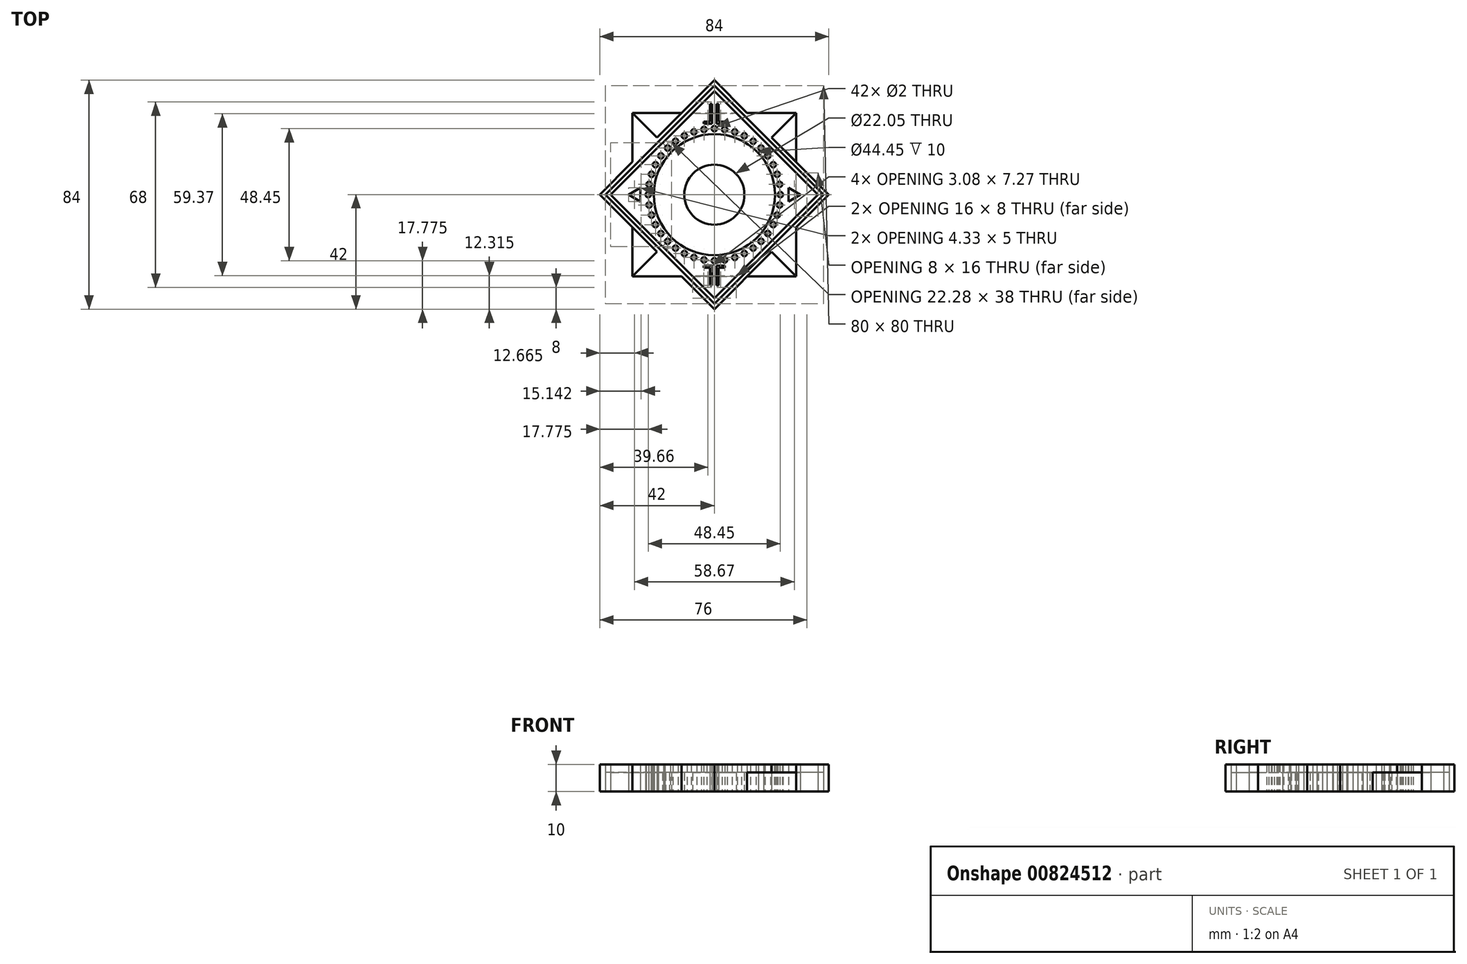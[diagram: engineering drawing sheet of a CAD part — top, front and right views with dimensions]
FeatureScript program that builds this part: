
annotation { "Feature Type Name" : "Feature", "Feature Type Description" : "" }
export const myFeature = defineFeature(function(context is Context, id is Id, definition is map)
    precondition{}
    {
        {
            var Q0;
            Q0=qCreatedBy(makeId("Top.planeOp"),FACE);
            var sketch = newSketch(context, id + "F0", { "sketchPlane" : qUnion([Q0])});
            skCircle(sketch, "E0", {"center": v(0, 0) * mm, "radius": 11.03 * mm});
            skCircle(sketch, "E1", {"center": v(0, 0) * mm, "radius": 22.23 * mm});
            skLineSegment(sketch, "E2.bottom", {"start": v(-30, -30) * mm, "end": v(30, -30) * mm});
            skLineSegment(sketch, "E2.top", {"start": v(-30, 30) * mm, "end": v(30, 30) * mm});
            skLineSegment(sketch, "E2.left", {"start": v(-30, -30) * mm, "end": v(-30, 30) * mm});
            skLineSegment(sketch, "E2.right", {"start": v(30, -30) * mm, "end": v(30, 30) * mm});
            skLineSegment(sketch, "E3", {"start": v(0, 42) * mm, "end": v(-42, 0) * mm});
            skLineSegment(sketch, "E4", {"start": v(-42, 0) * mm, "end": v(0, -42) * mm});
            skLineSegment(sketch, "E5", {"start": v(0, -42) * mm, "end": v(42, 0) * mm});
            skLineSegment(sketch, "E6", {"start": v(42, 0) * mm, "end": v(0, 42) * mm});
            skLineSegment(sketch, "E7", {"start": v(-30, 30) * mm, "end": v(30, -30) * mm});
            skLineSegment(sketch, "E8", {"start": v(-30, -30) * mm, "end": v(30, 30) * mm});
            skLineSegment(sketch, "E9", {"start": v(-40, 0) * mm, "end": v(0, 40) * mm});
            skLineSegment(sketch, "E10", {"start": v(0, 40) * mm, "end": v(40, 0) * mm});
            skLineSegment(sketch, "E11", {"start": v(40, 0) * mm, "end": v(0, -40) * mm});
            skLineSegment(sketch, "E12", {"start": v(0, -40) * mm, "end": v(-40, 0) * mm});
            skLineSegment(sketch, "E13", {"start": v(0, 38) * mm, "end": v(-38, 0) * mm});
            skPoint(sketch, "E13.startSnap0", {"position": v(0, 30) * mm});
            skPoint(sketch, "E13.endSnap0", {"position": v(-30, 0) * mm});
            skLineSegment(sketch, "E14", {"start": v(-38, 0) * mm, "end": v(0, -38) * mm});
            skLineSegment(sketch, "E15", {"start": v(0, -38) * mm, "end": v(38, 0) * mm});
            skLineSegment(sketch, "E16", {"start": v(38, 0) * mm, "end": v(0, 38) * mm});
            skCircle(sketch, "E17", {"center": v(0, 24.23) * mm, "radius": 1 * mm});
            skCircle(sketch, "E18.1.0", {"center": v(-3.79, 23.93) * mm, "radius": 1 * mm});
            skCircle(sketch, "E18.2.0", {"center": v(-7.49, 23.04) * mm, "radius": 1 * mm});
            skCircle(sketch, "E18.3.0", {"center": v(-11, 21.58) * mm, "radius": 1 * mm});
            skCircle(sketch, "E18.4.0", {"center": v(-14.24, 19.6) * mm, "radius": 1 * mm});
            skCircle(sketch, "E18.5.0", {"center": v(-17.13, 17.13) * mm, "radius": 1 * mm});
            skCircle(sketch, "E18.6.0", {"center": v(-19.6, 14.24) * mm, "radius": 1 * mm});
            skCircle(sketch, "E18.7.0", {"center": v(-21.58, 11) * mm, "radius": 1 * mm});
            skCircle(sketch, "E18.8.0", {"center": v(-23.04, 7.49) * mm, "radius": 1 * mm});
            skCircle(sketch, "E18.9.0", {"center": v(-23.93, 3.79) * mm, "radius": 1 * mm});
            skCircle(sketch, "E18.10.0", {"center": v(-24.23, 0) * mm, "radius": 1 * mm});
            skCircle(sketch, "E18.11.0", {"center": v(-23.93, -3.79) * mm, "radius": 1 * mm});
            skCircle(sketch, "E18.12.0", {"center": v(-23.04, -7.49) * mm, "radius": 1 * mm});
            skCircle(sketch, "E18.13.0", {"center": v(-21.58, -11) * mm, "radius": 1 * mm});
            skCircle(sketch, "E18.14.0", {"center": v(-19.6, -14.24) * mm, "radius": 1 * mm});
            skCircle(sketch, "E18.15.0", {"center": v(-17.13, -17.13) * mm, "radius": 1 * mm});
            skCircle(sketch, "E18.16.0", {"center": v(-14.24, -19.6) * mm, "radius": 1 * mm});
            skCircle(sketch, "E18.17.0", {"center": v(-11, -21.58) * mm, "radius": 1 * mm});
            skCircle(sketch, "E18.18.0", {"center": v(-7.49, -23.04) * mm, "radius": 1 * mm});
            skCircle(sketch, "E18.19.0", {"center": v(-3.79, -23.93) * mm, "radius": 1 * mm});
            skCircle(sketch, "E18.20.0", {"center": v(0, -24.23) * mm, "radius": 1 * mm});
            skCircle(sketch, "E18.21.0", {"center": v(3.79, -23.93) * mm, "radius": 1 * mm});
            skCircle(sketch, "E18.22.0", {"center": v(7.49, -23.04) * mm, "radius": 1 * mm});
            skCircle(sketch, "E18.23.0", {"center": v(11, -21.58) * mm, "radius": 1 * mm});
            skCircle(sketch, "E18.24.0", {"center": v(14.24, -19.6) * mm, "radius": 1 * mm});
            skCircle(sketch, "E18.25.0", {"center": v(17.13, -17.13) * mm, "radius": 1 * mm});
            skCircle(sketch, "E18.26.0", {"center": v(19.6, -14.24) * mm, "radius": 1 * mm});
            skCircle(sketch, "E18.27.0", {"center": v(21.58, -11) * mm, "radius": 1 * mm});
            skCircle(sketch, "E18.28.0", {"center": v(23.04, -7.49) * mm, "radius": 1 * mm});
            skCircle(sketch, "E18.29.0", {"center": v(23.93, -3.79) * mm, "radius": 1 * mm});
            skCircle(sketch, "E18.30.0", {"center": v(24.23, 0) * mm, "radius": 1 * mm});
            skCircle(sketch, "E18.31.0", {"center": v(23.93, 3.79) * mm, "radius": 1 * mm});
            skCircle(sketch, "E18.32.0", {"center": v(23.04, 7.49) * mm, "radius": 1 * mm});
            skCircle(sketch, "E18.33.0", {"center": v(21.58, 11) * mm, "radius": 1 * mm});
            skCircle(sketch, "E18.34.0", {"center": v(19.6, 14.24) * mm, "radius": 1 * mm});
            skCircle(sketch, "E18.35.0", {"center": v(17.13, 17.13) * mm, "radius": 1 * mm});
            skCircle(sketch, "E18.36.0", {"center": v(14.24, 19.6) * mm, "radius": 1 * mm});
            skCircle(sketch, "E18.37.0", {"center": v(11, 21.58) * mm, "radius": 1 * mm});
            skCircle(sketch, "E18.38.0", {"center": v(7.49, 23.04) * mm, "radius": 1 * mm});
            skCircle(sketch, "E18.39.0", {"center": v(3.79, 23.93) * mm, "radius": 1 * mm});
            skLineSegment(sketch, "E19", {"start": v(-31.5, 0) * mm, "end": v(-27.17, 2.5) * mm});
            skLineSegment(sketch, "E20", {"start": v(-27.17, 2.5) * mm, "end": v(-27.17, -2.5) * mm});
            skLineSegment(sketch, "E21", {"start": v(-27.17, -2.5) * mm, "end": v(-31.5, 0) * mm});
            skLineSegment(sketch, "E22.1.0", {"start": v(27.17, -2.5) * mm, "end": v(27.17, 2.5) * mm});
            skLineSegment(sketch, "E22.1.1", {"start": v(31.5, 0) * mm, "end": v(27.17, -2.5) * mm});
            skLineSegment(sketch, "E22.1.2", {"start": v(27.17, 2.5) * mm, "end": v(31.5, 0) * mm});
            skLineSegment(sketch, "E23", {"start": v(-3.88, -26.05) * mm, "end": v(-0.8, -26.05) * mm});
            skLineSegment(sketch, "E24", {"start": v(-0.8, -26.05) * mm, "end": v(-0.8, -33.32) * mm});
            skLineSegment(sketch, "E25", {"start": v(-0.8, -33.32) * mm, "end": v(-1.6, -33.32) * mm});
            skLineSegment(sketch, "E26", {"start": v(-3.88, -26.05) * mm, "end": v(-3.88, -26.85) * mm});
            skLineSegment(sketch, "E27", {"start": v(-3.88, -26.85) * mm, "end": v(-1.6, -26.85) * mm});
            skLineSegment(sketch, "E28", {"start": v(-1.6, -26.85) * mm, "end": v(-1.6, -33.32) * mm});
            skLineSegment(sketch, "E29.MirrorCS", {"start": v(0.8, -33.32) * mm, "end": v(1.6, -33.32) * mm});
            skLineSegment(sketch, "E30.MirrorCS", {"start": v(0.8, -26.05) * mm, "end": v(0.8, -33.32) * mm});
            skLineSegment(sketch, "E31.MirrorCS", {"start": v(3.88, -26.05) * mm, "end": v(0.8, -26.05) * mm});
            skLineSegment(sketch, "E32.MirrorCS", {"start": v(3.88, -26.05) * mm, "end": v(3.88, -26.85) * mm});
            skLineSegment(sketch, "E33.MirrorCS", {"start": v(1.6, -26.85) * mm, "end": v(1.6, -33.32) * mm});
            skLineSegment(sketch, "E34.MirrorCS", {"start": v(3.88, -26.85) * mm, "end": v(1.6, -26.85) * mm});
            skLineSegment(sketch, "E35.MirrorCS", {"start": v(3.88, 26.05) * mm, "end": v(0.8, 26.05) * mm});
            skLineSegment(sketch, "E36.MirrorCS", {"start": v(3.88, 26.05) * mm, "end": v(3.88, 26.85) * mm});
            skLineSegment(sketch, "E37.MirrorCS", {"start": v(3.88, 26.85) * mm, "end": v(1.6, 26.85) * mm});
            skLineSegment(sketch, "E38.MirrorCS", {"start": v(1.6, 26.85) * mm, "end": v(1.6, 33.32) * mm});
            skLineSegment(sketch, "E39.MirrorCS", {"start": v(0.8, 26.05) * mm, "end": v(0.8, 33.32) * mm});
            skLineSegment(sketch, "E40.MirrorCS", {"start": v(0.8, 33.32) * mm, "end": v(1.6, 33.32) * mm});
            skLineSegment(sketch, "E41.MirrorCS", {"start": v(-0.8, 33.32) * mm, "end": v(-1.6, 33.32) * mm});
            skLineSegment(sketch, "E42.MirrorCS", {"start": v(-1.6, 26.85) * mm, "end": v(-1.6, 33.32) * mm});
            skLineSegment(sketch, "E43.MirrorCS", {"start": v(-0.8, 26.05) * mm, "end": v(-0.8, 33.32) * mm});
            skLineSegment(sketch, "E44.MirrorCS", {"start": v(-3.88, 26.05) * mm, "end": v(-0.8, 26.05) * mm});
            skLineSegment(sketch, "E45.MirrorCS", {"start": v(-3.88, 26.85) * mm, "end": v(-1.6, 26.85) * mm});
            skLineSegment(sketch, "E46.MirrorCS", {"start": v(-3.88, 26.05) * mm, "end": v(-3.88, 26.85) * mm});
            skSolve(sketch);
        }
        {
            var Q0;
            Q0=makeQuery(id+"F0.imprint","IMPRINT",FACE,{"disambiguationData":[TD([[makeQuery(id+"F0.imprint","IMPRINT",EDGE,{"derivedFrom":sQuery(id+"F0.wireOp",EDGE,"E18.6.0")}),-1.0]])]});
            var Q1;
            {var subQ0=sQuery(id+"F0.wireOp",EDGE,"E14");var subQ3=sQuery(id+"F0.wireOp",EDGE,"E2.left");var subQ4=makeQuery(id+"F0.imprint","INTERSECT",VERTEX,{"derivedFrom":[subQ3,subQ0]});Q1=makeQuery(id+"F0.imprint","IMPRINT",FACE,{"disambiguationData":[TD([[makeQuery(id+"F0.imprint","IMPRINT",EDGE,{"disambiguationData":[TD([[subQ4,-1.0]])],"derivedFrom":subQ3}),1.0]])]});}
            var Q2;
            Q2=makeQuery(id+"F0.imprint","IMPRINT",FACE,{"disambiguationData":[TD([[makeQuery(id+"F0.imprint","IMPRINT",EDGE,{"derivedFrom":sQuery(id+"F0.wireOp",EDGE,"E17")}),-1.0]])]});
            var Q3;
            Q3=makeQuery(id+"F0.imprint","IMPRINT",FACE,{"disambiguationData":[TD([[makeQuery(id+"F0.imprint","IMPRINT",EDGE,{"derivedFrom":sQuery(id+"F0.wireOp",EDGE,"E18.26.0")}),-1.0]])]});
            var Q4;
            {var subQ1=sQuery(id+"F0.wireOp",EDGE,"E15");var subQ3=sQuery(id+"F0.wireOp",EDGE,"E2.right");var subQ4=makeQuery(id+"F0.imprint","INTERSECT",VERTEX,{"derivedFrom":[subQ3,subQ1]});Q4=makeQuery(id+"F0.imprint","IMPRINT",FACE,{"disambiguationData":[TD([[makeQuery(id+"F0.imprint","IMPRINT",EDGE,{"disambiguationData":[TD([[subQ4,-1.0]])],"derivedFrom":subQ3}),-1.0]])]});}
            var Q5;
            Q5=makeQuery(id+"F0.imprint","IMPRINT",FACE,{"disambiguationData":[TD([[makeQuery(id+"F0.imprint","IMPRINT",EDGE,{"derivedFrom":sQuery(id+"F0.wireOp",EDGE,"E18.16.0")}),-1.0]])]});
            var Q6;
            {var subQ4=sQuery(id+"F0.wireOp",EDGE,"E25");Q6=makeQuery(id+"F0.imprint","IMPRINT",FACE,{"disambiguationData":[TD([[makeQuery(id+"F0.imprint","IMPRINT",EDGE,{"derivedFrom":subQ4}),1.0]])]});}
            var Q7;
            {var subQ10=sQuery(id+"F0.wireOp",EDGE,"E40.MirrorCS");Q7=makeQuery(id+"F0.imprint","IMPRINT",FACE,{"disambiguationData":[TD([[makeQuery(id+"F0.imprint","IMPRINT",EDGE,{"derivedFrom":subQ10}),1.0]])]});}
            var Q8;
            {var subQ0=sQuery(id+"F0.wireOp",EDGE,"E3");var subQ1=sQuery(id+"F0.wireOp",EDGE,"E2.left");var subQ2=makeQuery(id+"F0.imprint","INTERSECT",VERTEX,{"derivedFrom":[subQ1,subQ0]});Q8=makeQuery(id+"F0.imprint","IMPRINT",FACE,{"disambiguationData":[TD([[makeQuery(id+"F0.imprint","IMPRINT",EDGE,{"disambiguationData":[TD([[subQ2,1.0]])],"derivedFrom":subQ1}),-1.0]])]});}
            var Q9;
            {var subQ0=sQuery(id+"F0.wireOp",EDGE,"E4");var subQ3=sQuery(id+"F0.wireOp",EDGE,"E2.left");var subQ4=makeQuery(id+"F0.imprint","INTERSECT",VERTEX,{"derivedFrom":[subQ3,subQ0]});Q9=makeQuery(id+"F0.imprint","IMPRINT",FACE,{"disambiguationData":[TD([[makeQuery(id+"F0.imprint","IMPRINT",EDGE,{"disambiguationData":[TD([[subQ4,-1.0]])],"derivedFrom":subQ3}),1.0]])]});}
            var Q10;
            {var subQ0=sQuery(id+"F0.wireOp",EDGE,"E4");var subQ1=sQuery(id+"F0.wireOp",EDGE,"E2.left");var subQ2=makeQuery(id+"F0.imprint","INTERSECT",VERTEX,{"derivedFrom":[subQ1,subQ0]});Q10=makeQuery(id+"F0.imprint","IMPRINT",FACE,{"disambiguationData":[TD([[makeQuery(id+"F0.imprint","IMPRINT",EDGE,{"disambiguationData":[TD([[subQ2,-1.0]])],"derivedFrom":subQ1}),-1.0]])]});}
            var Q11;
            {var subQ0=sQuery(id+"F0.wireOp",EDGE,"E4");var subQ1=sQuery(id+"F0.wireOp",EDGE,"E2.bottom");var subQ2=makeQuery(id+"F0.imprint","INTERSECT",VERTEX,{"derivedFrom":[subQ1,subQ0]});Q11=makeQuery(id+"F0.imprint","IMPRINT",FACE,{"disambiguationData":[TD([[makeQuery(id+"F0.imprint","IMPRINT",EDGE,{"disambiguationData":[TD([[subQ2,-1.0]])],"derivedFrom":subQ1}),1.0]])]});}
            var Q12;
            {var subQ1=sQuery(id+"F0.wireOp",EDGE,"E4");var subQ3=sQuery(id+"F0.wireOp",EDGE,"E2.bottom");var subQ5=makeQuery(id+"F0.imprint","INTERSECT",VERTEX,{"derivedFrom":[subQ3,subQ1]});Q12=makeQuery(id+"F0.imprint","IMPRINT",FACE,{"disambiguationData":[TD([[makeQuery(id+"F0.imprint","IMPRINT",EDGE,{"disambiguationData":[TD([[subQ5,-1.0]])],"derivedFrom":subQ3}),-1.0]])]});}
            var Q13;
            {var subQ0=sQuery(id+"F0.wireOp",EDGE,"E5");var subQ1=sQuery(id+"F0.wireOp",EDGE,"E2.right");var subQ2=makeQuery(id+"F0.imprint","INTERSECT",VERTEX,{"derivedFrom":[subQ1,subQ0]});Q13=makeQuery(id+"F0.imprint","IMPRINT",FACE,{"disambiguationData":[TD([[makeQuery(id+"F0.imprint","IMPRINT",EDGE,{"disambiguationData":[TD([[subQ2,-1.0]])],"derivedFrom":subQ1}),1.0]])]});}
            var Q14;
            {var subQ0=sQuery(id+"F0.wireOp",EDGE,"E5");var subQ1=sQuery(id+"F0.wireOp",EDGE,"E2.bottom");var subQ2=makeQuery(id+"F0.imprint","INTERSECT",VERTEX,{"derivedFrom":[subQ1,subQ0]});Q14=makeQuery(id+"F0.imprint","IMPRINT",FACE,{"disambiguationData":[TD([[makeQuery(id+"F0.imprint","IMPRINT",EDGE,{"disambiguationData":[TD([[subQ2,1.0]])],"derivedFrom":subQ1}),1.0]])]});}
            var Q15;
            {var subQ1=sQuery(id+"F0.wireOp",EDGE,"E5");var subQ3=sQuery(id+"F0.wireOp",EDGE,"E2.right");var subQ4=makeQuery(id+"F0.imprint","INTERSECT",VERTEX,{"derivedFrom":[subQ3,subQ1]});Q15=makeQuery(id+"F0.imprint","IMPRINT",FACE,{"disambiguationData":[TD([[makeQuery(id+"F0.imprint","IMPRINT",EDGE,{"disambiguationData":[TD([[subQ4,-1.0]])],"derivedFrom":subQ3}),-1.0]])]});}
            var Q16;
            {var subQ0=sQuery(id+"F0.wireOp",EDGE,"E6");var subQ1=sQuery(id+"F0.wireOp",EDGE,"E2.right");var subQ2=makeQuery(id+"F0.imprint","INTERSECT",VERTEX,{"derivedFrom":[subQ1,subQ0]});Q16=makeQuery(id+"F0.imprint","IMPRINT",FACE,{"disambiguationData":[TD([[makeQuery(id+"F0.imprint","IMPRINT",EDGE,{"disambiguationData":[TD([[subQ2,1.0]])],"derivedFrom":subQ1}),1.0]])]});}
            var Q17;
            {var subQ0=sQuery(id+"F0.wireOp",EDGE,"E6");var subQ1=sQuery(id+"F0.wireOp",EDGE,"E2.top");var subQ2=makeQuery(id+"F0.imprint","INTERSECT",VERTEX,{"derivedFrom":[subQ1,subQ0]});Q17=makeQuery(id+"F0.imprint","IMPRINT",FACE,{"disambiguationData":[TD([[makeQuery(id+"F0.imprint","IMPRINT",EDGE,{"disambiguationData":[TD([[subQ2,1.0]])],"derivedFrom":subQ1}),-1.0]])]});}
            var Q18;
            {var subQ1=sQuery(id+"F0.wireOp",EDGE,"E3");var subQ3=sQuery(id+"F0.wireOp",EDGE,"E2.top");var subQ5=makeQuery(id+"F0.imprint","INTERSECT",VERTEX,{"derivedFrom":[subQ3,subQ1]});Q18=makeQuery(id+"F0.imprint","IMPRINT",FACE,{"disambiguationData":[TD([[makeQuery(id+"F0.imprint","IMPRINT",EDGE,{"disambiguationData":[TD([[subQ5,-1.0]])],"derivedFrom":subQ3}),1.0]])]});}
            var Q19;
            {var subQ0=sQuery(id+"F0.wireOp",EDGE,"E3");var subQ1=sQuery(id+"F0.wireOp",EDGE,"E2.top");var subQ2=makeQuery(id+"F0.imprint","INTERSECT",VERTEX,{"derivedFrom":[subQ1,subQ0]});Q19=makeQuery(id+"F0.imprint","IMPRINT",FACE,{"disambiguationData":[TD([[makeQuery(id+"F0.imprint","IMPRINT",EDGE,{"disambiguationData":[TD([[subQ2,-1.0]])],"derivedFrom":subQ1}),-1.0]])]});}
            var Q20;
            {var subQ1=sQuery(id+"F0.wireOp",EDGE,"E2.left");var subQ3=sQuery(id+"F0.wireOp",EDGE,"E3");var subQ4=makeQuery(id+"F0.imprint","INTERSECT",VERTEX,{"derivedFrom":[subQ1,subQ3]});Q20=makeQuery(id+"F0.imprint","IMPRINT",FACE,{"disambiguationData":[TD([[makeQuery(id+"F0.imprint","IMPRINT",EDGE,{"disambiguationData":[TD([[subQ4,1.0]])],"derivedFrom":subQ3}),-1.0]])]});}
            var Q21;
            {var subQ1=sQuery(id+"F0.wireOp",EDGE,"E2.top");var subQ3=sQuery(id+"F0.wireOp",EDGE,"E6");var subQ4=makeQuery(id+"F0.imprint","INTERSECT",VERTEX,{"derivedFrom":[subQ1,subQ3]});Q21=makeQuery(id+"F0.imprint","IMPRINT",FACE,{"disambiguationData":[TD([[makeQuery(id+"F0.imprint","IMPRINT",EDGE,{"disambiguationData":[TD([[subQ4,1.0]])],"derivedFrom":subQ3}),-1.0]])]});}
            var Q22;
            {var subQ1=sQuery(id+"F0.wireOp",EDGE,"E2.right");var subQ3=sQuery(id+"F0.wireOp",EDGE,"E5");var subQ4=makeQuery(id+"F0.imprint","INTERSECT",VERTEX,{"derivedFrom":[subQ1,subQ3]});Q22=makeQuery(id+"F0.imprint","IMPRINT",FACE,{"disambiguationData":[TD([[makeQuery(id+"F0.imprint","IMPRINT",EDGE,{"disambiguationData":[TD([[subQ4,1.0]])],"derivedFrom":subQ3}),-1.0]])]});}
            var Q23;
            {var subQ1=sQuery(id+"F0.wireOp",EDGE,"E2.bottom");var subQ3=sQuery(id+"F0.wireOp",EDGE,"E4");var subQ4=makeQuery(id+"F0.imprint","INTERSECT",VERTEX,{"derivedFrom":[subQ1,subQ3]});Q23=makeQuery(id+"F0.imprint","IMPRINT",FACE,{"disambiguationData":[TD([[makeQuery(id+"F0.imprint","IMPRINT",EDGE,{"disambiguationData":[TD([[subQ4,1.0]])],"derivedFrom":subQ3}),-1.0]])]});}
            extrude(context, id + "F1", {"entities" : qUnion([Q0, Q1, Q2, Q3, Q4, Q5, Q6, Q7, Q8, Q9, Q10, Q11, Q12, Q13, Q14, Q15, Q16, Q17, Q18, Q19, Q20, Q21, Q22, Q23]), "depth" : 10 * mm, "offsetDistance" : 25 * mm});
        }
        {
            var Q0;
            {var subQ1=sQuery(id+"F0.wireOp",EDGE,"E2.bottom");var subQ3=sQuery(id+"F0.wireOp",EDGE,"E5");var subQ4=makeQuery(id+"F0.imprint","INTERSECT",VERTEX,{"derivedFrom":[subQ1,subQ3]});Q0=makeQuery(id+"F0.imprint","IMPRINT",FACE,{"disambiguationData":[TD([[makeQuery(id+"F0.imprint","IMPRINT",EDGE,{"disambiguationData":[TD([[subQ4,-1.0]])],"derivedFrom":subQ3}),-1.0]])]});}
            var Q1;
            {var subQ1=sQuery(id+"F0.wireOp",EDGE,"E2.left");var subQ3=sQuery(id+"F0.wireOp",EDGE,"E4");var subQ4=makeQuery(id+"F0.imprint","INTERSECT",VERTEX,{"derivedFrom":[subQ1,subQ3]});Q1=makeQuery(id+"F0.imprint","IMPRINT",FACE,{"disambiguationData":[TD([[makeQuery(id+"F0.imprint","IMPRINT",EDGE,{"disambiguationData":[TD([[subQ4,-1.0]])],"derivedFrom":subQ3}),-1.0]])]});}
            var Q2;
            {var subQ0=sQuery(id+"F0.wireOp",EDGE,"E11");var subQ1=sQuery(id+"F0.wireOp",EDGE,"E2.right");var subQ2=makeQuery(id+"F0.imprint","INTERSECT",VERTEX,{"derivedFrom":[subQ1,subQ0]});Q2=makeQuery(id+"F0.imprint","IMPRINT",FACE,{"disambiguationData":[TD([[makeQuery(id+"F0.imprint","IMPRINT",EDGE,{"disambiguationData":[TD([[subQ2,-1.0]])],"derivedFrom":subQ1}),1.0]])]});}
            var Q3;
            {var subQ0=sQuery(id+"F0.wireOp",EDGE,"E11");var subQ3=sQuery(id+"F0.wireOp",EDGE,"E2.right");var subQ4=makeQuery(id+"F0.imprint","INTERSECT",VERTEX,{"derivedFrom":[subQ3,subQ0]});Q3=makeQuery(id+"F0.imprint","IMPRINT",FACE,{"disambiguationData":[TD([[makeQuery(id+"F0.imprint","IMPRINT",EDGE,{"disambiguationData":[TD([[subQ4,-1.0]])],"derivedFrom":subQ3}),-1.0]])]});}
            var Q4;
            {var subQ0=sQuery(id+"F0.wireOp",EDGE,"E16");var subQ1=sQuery(id+"F0.wireOp",EDGE,"E2.right");var subQ2=makeQuery(id+"F0.imprint","INTERSECT",VERTEX,{"derivedFrom":[subQ1,subQ0]});Q4=makeQuery(id+"F0.imprint","IMPRINT",FACE,{"disambiguationData":[TD([[makeQuery(id+"F0.imprint","IMPRINT",EDGE,{"disambiguationData":[TD([[subQ2,-1.0]])],"derivedFrom":subQ1}),1.0]])]});}
            var Q5;
            {var subQ0=sQuery(id+"F0.wireOp",EDGE,"E16");var subQ1=sQuery(id+"F0.wireOp",EDGE,"E2.top");var subQ2=makeQuery(id+"F0.imprint","INTERSECT",VERTEX,{"derivedFrom":[subQ1,subQ0]});Q5=makeQuery(id+"F0.imprint","IMPRINT",FACE,{"disambiguationData":[TD([[makeQuery(id+"F0.imprint","IMPRINT",EDGE,{"disambiguationData":[TD([[subQ2,-1.0]])],"derivedFrom":subQ1}),-1.0]])]});}
            var Q6;
            {var subQ1=sQuery(id+"F0.wireOp",EDGE,"E9");var subQ3=sQuery(id+"F0.wireOp",EDGE,"E2.top");var subQ5=makeQuery(id+"F0.imprint","INTERSECT",VERTEX,{"derivedFrom":[subQ3,subQ1]});Q6=makeQuery(id+"F0.imprint","IMPRINT",FACE,{"disambiguationData":[TD([[makeQuery(id+"F0.imprint","IMPRINT",EDGE,{"disambiguationData":[TD([[subQ5,-1.0]])],"derivedFrom":subQ3}),1.0]])]});}
            var Q7;
            {var subQ0=sQuery(id+"F0.wireOp",EDGE,"E9");var subQ1=sQuery(id+"F0.wireOp",EDGE,"E2.top");var subQ2=makeQuery(id+"F0.imprint","INTERSECT",VERTEX,{"derivedFrom":[subQ1,subQ0]});Q7=makeQuery(id+"F0.imprint","IMPRINT",FACE,{"disambiguationData":[TD([[makeQuery(id+"F0.imprint","IMPRINT",EDGE,{"disambiguationData":[TD([[subQ2,-1.0]])],"derivedFrom":subQ1}),-1.0]])]});}
            var Q8;
            {var subQ0=sQuery(id+"F0.wireOp",EDGE,"E13");var subQ1=sQuery(id+"F0.wireOp",EDGE,"E2.left");var subQ2=makeQuery(id+"F0.imprint","INTERSECT",VERTEX,{"derivedFrom":[subQ1,subQ0]});Q8=makeQuery(id+"F0.imprint","IMPRINT",FACE,{"disambiguationData":[TD([[makeQuery(id+"F0.imprint","IMPRINT",EDGE,{"disambiguationData":[TD([[subQ2,-1.0]])],"derivedFrom":subQ1}),-1.0]])]});}
            var Q9;
            {var subQ0=sQuery(id+"F0.wireOp",EDGE,"E12");var subQ3=sQuery(id+"F0.wireOp",EDGE,"E2.left");var subQ4=makeQuery(id+"F0.imprint","INTERSECT",VERTEX,{"derivedFrom":[subQ3,subQ0]});Q9=makeQuery(id+"F0.imprint","IMPRINT",FACE,{"disambiguationData":[TD([[makeQuery(id+"F0.imprint","IMPRINT",EDGE,{"disambiguationData":[TD([[subQ4,-1.0]])],"derivedFrom":subQ3}),1.0]])]});}
            var Q10;
            {var subQ0=sQuery(id+"F0.wireOp",EDGE,"E12");var subQ1=sQuery(id+"F0.wireOp",EDGE,"E2.left");var subQ2=makeQuery(id+"F0.imprint","INTERSECT",VERTEX,{"derivedFrom":[subQ1,subQ0]});Q10=makeQuery(id+"F0.imprint","IMPRINT",FACE,{"disambiguationData":[TD([[makeQuery(id+"F0.imprint","IMPRINT",EDGE,{"disambiguationData":[TD([[subQ2,-1.0]])],"derivedFrom":subQ1}),-1.0]])]});}
            var Q11;
            {var subQ0=sQuery(id+"F0.wireOp",EDGE,"E12");var subQ1=sQuery(id+"F0.wireOp",EDGE,"E2.bottom");var subQ2=makeQuery(id+"F0.imprint","INTERSECT",VERTEX,{"derivedFrom":[subQ1,subQ0]});Q11=makeQuery(id+"F0.imprint","IMPRINT",FACE,{"disambiguationData":[TD([[makeQuery(id+"F0.imprint","IMPRINT",EDGE,{"disambiguationData":[TD([[subQ2,-1.0]])],"derivedFrom":subQ1}),1.0]])]});}
            var Q12;
            {var subQ0=sQuery(id+"F0.wireOp",EDGE,"E15");var subQ1=sQuery(id+"F0.wireOp",EDGE,"E2.bottom");var subQ2=makeQuery(id+"F0.imprint","INTERSECT",VERTEX,{"derivedFrom":[subQ1,subQ0]});Q12=makeQuery(id+"F0.imprint","IMPRINT",FACE,{"disambiguationData":[TD([[makeQuery(id+"F0.imprint","IMPRINT",EDGE,{"disambiguationData":[TD([[subQ2,-1.0]])],"derivedFrom":subQ1}),1.0]])]});}
            var Q13;
            {var subQ0=sQuery(id+"F0.wireOp",EDGE,"E12");var subQ3=sQuery(id+"F0.wireOp",EDGE,"E2.bottom");var subQ4=makeQuery(id+"F0.imprint","INTERSECT",VERTEX,{"derivedFrom":[subQ3,subQ0]});Q13=makeQuery(id+"F0.imprint","IMPRINT",FACE,{"disambiguationData":[TD([[makeQuery(id+"F0.imprint","IMPRINT",EDGE,{"disambiguationData":[TD([[subQ4,-1.0]])],"derivedFrom":subQ3}),-1.0]])]});}
            var Q14;
            {var subQ0=sQuery(id+"F0.wireOp",EDGE,"E31.MirrorCS");Q14=makeQuery(id+"F0.imprint","IMPRINT",FACE,{"disambiguationData":[TD([[makeQuery(id+"F0.imprint","IMPRINT",EDGE,{"derivedFrom":subQ0}),1.0]])]});}
            var Q15;
            {var subQ1=sQuery(id+"F0.wireOp",EDGE,"E23");Q15=makeQuery(id+"F0.imprint","IMPRINT",FACE,{"disambiguationData":[TD([[makeQuery(id+"F0.imprint","IMPRINT",EDGE,{"derivedFrom":subQ1}),-1.0]])]});}
            var Q16;
            {var subQ5=sQuery(id+"F0.wireOp",EDGE,"E25");Q16=makeQuery(id+"F0.imprint","IMPRINT",FACE,{"disambiguationData":[TD([[makeQuery(id+"F0.imprint","IMPRINT",EDGE,{"derivedFrom":subQ5}),-1.0]])]});}
            var Q17;
            {var subQ5=sQuery(id+"F0.wireOp",EDGE,"E29.MirrorCS");Q17=makeQuery(id+"F0.imprint","IMPRINT",FACE,{"disambiguationData":[TD([[makeQuery(id+"F0.imprint","IMPRINT",EDGE,{"derivedFrom":subQ5}),1.0]])]});}
            var Q18;
            {var subQ5=sQuery(id+"F0.wireOp",EDGE,"E22.1.0");Q18=makeQuery(id+"F0.imprint","IMPRINT",FACE,{"disambiguationData":[TD([[makeQuery(id+"F0.imprint","IMPRINT",EDGE,{"derivedFrom":subQ5}),-1.0]])]});}
            var Q19;
            {var subQ5=sQuery(id+"F0.wireOp",EDGE,"E20");Q19=makeQuery(id+"F0.imprint","IMPRINT",FACE,{"disambiguationData":[TD([[makeQuery(id+"F0.imprint","IMPRINT",EDGE,{"derivedFrom":subQ5}),-1.0]])]});}
            var Q20;
            {var subQ0=sQuery(id+"F0.wireOp",EDGE,"E21");var subQ1=sQuery(id+"F0.wireOp",EDGE,"E2.left");var subQ2=makeQuery(id+"F0.imprint","INTERSECT",VERTEX,{"derivedFrom":[subQ1,subQ0]});Q20=makeQuery(id+"F0.imprint","IMPRINT",FACE,{"disambiguationData":[TD([[makeQuery(id+"F0.imprint","IMPRINT",EDGE,{"disambiguationData":[TD([[subQ2,-1.0]])],"derivedFrom":subQ1}),1.0]])]});}
            var Q21;
            {var subQ0=sQuery(id+"F0.wireOp",EDGE,"E22.1.1");var subQ1=sQuery(id+"F0.wireOp",EDGE,"E2.right");var subQ2=makeQuery(id+"F0.imprint","INTERSECT",VERTEX,{"derivedFrom":[subQ1,subQ0]});Q21=makeQuery(id+"F0.imprint","IMPRINT",FACE,{"disambiguationData":[TD([[makeQuery(id+"F0.imprint","IMPRINT",EDGE,{"disambiguationData":[TD([[subQ2,-1.0]])],"derivedFrom":subQ1}),-1.0]])]});}
            var Q22;
            {var subQ0=sQuery(id+"F0.wireOp",EDGE,"E35.MirrorCS");Q22=makeQuery(id+"F0.imprint","IMPRINT",FACE,{"disambiguationData":[TD([[makeQuery(id+"F0.imprint","IMPRINT",EDGE,{"derivedFrom":subQ0}),-1.0]])]});}
            var Q23;
            {var subQ0=sQuery(id+"F0.wireOp",EDGE,"E44.MirrorCS");Q23=makeQuery(id+"F0.imprint","IMPRINT",FACE,{"disambiguationData":[TD([[makeQuery(id+"F0.imprint","IMPRINT",EDGE,{"derivedFrom":subQ0}),1.0]])]});}
            var Q24;
            {var subQ5=sQuery(id+"F0.wireOp",EDGE,"E41.MirrorCS");Q24=makeQuery(id+"F0.imprint","IMPRINT",FACE,{"disambiguationData":[TD([[makeQuery(id+"F0.imprint","IMPRINT",EDGE,{"derivedFrom":subQ5}),1.0]])]});}
            var Q25;
            {var subQ5=sQuery(id+"F0.wireOp",EDGE,"E40.MirrorCS");Q25=makeQuery(id+"F0.imprint","IMPRINT",FACE,{"disambiguationData":[TD([[makeQuery(id+"F0.imprint","IMPRINT",EDGE,{"derivedFrom":subQ5}),-1.0]])]});}
            var Q26;
            {var subQ1=sQuery(id+"F0.wireOp",EDGE,"E2.top");var subQ3=sQuery(id+"F0.wireOp",EDGE,"E3");var subQ4=makeQuery(id+"F0.imprint","INTERSECT",VERTEX,{"derivedFrom":[subQ1,subQ3]});Q26=makeQuery(id+"F0.imprint","IMPRINT",FACE,{"disambiguationData":[TD([[makeQuery(id+"F0.imprint","IMPRINT",EDGE,{"disambiguationData":[TD([[subQ4,-1.0]])],"derivedFrom":subQ3}),-1.0]])]});}
            var Q27;
            {var subQ1=sQuery(id+"F0.wireOp",EDGE,"E2.right");var subQ3=sQuery(id+"F0.wireOp",EDGE,"E6");var subQ4=makeQuery(id+"F0.imprint","INTERSECT",VERTEX,{"derivedFrom":[subQ1,subQ3]});Q27=makeQuery(id+"F0.imprint","IMPRINT",FACE,{"disambiguationData":[TD([[makeQuery(id+"F0.imprint","IMPRINT",EDGE,{"disambiguationData":[TD([[subQ4,-1.0]])],"derivedFrom":subQ3}),-1.0]])]});}
            var Q28;
            Q28=makeQuery(id+"F0.imprint","IMPRINT",FACE,{"disambiguationData":[TD([[makeQuery(id+"F0.imprint","IMPRINT",EDGE,{"derivedFrom":sQuery(id+"F0.wireOp",EDGE,"E17")}),1.0]])]});
            var Q29;
            Q29=makeQuery(id+"F0.imprint","IMPRINT",FACE,{"disambiguationData":[TD([[makeQuery(id+"F0.imprint","IMPRINT",EDGE,{"derivedFrom":sQuery(id+"F0.wireOp",EDGE,"E18.1.0")}),1.0]])]});
            var Q30;
            Q30=makeQuery(id+"F0.imprint","IMPRINT",FACE,{"disambiguationData":[TD([[makeQuery(id+"F0.imprint","IMPRINT",EDGE,{"derivedFrom":sQuery(id+"F0.wireOp",EDGE,"E18.2.0")}),1.0]])]});
            var Q31;
            {var subQ0=sQuery(id+"F0.wireOp",EDGE,"E18.5.0");var subQ1=sQuery(id+"F0.wireOp",EDGE,"E7");var subQ2=makeQuery(id+"F0.imprint","INTERSECT",VERTEX,{"disambiguationData":[OD(0.0)],"derivedFrom":[subQ1,subQ0]});Q31=makeQuery(id+"F0.imprint","IMPRINT",FACE,{"disambiguationData":[TD([[makeQuery(id+"F0.imprint","IMPRINT",EDGE,{"disambiguationData":[TD([[subQ2,-1.0]])],"derivedFrom":subQ1}),-1.0]])]});}
            var Q32;
            Q32=makeQuery(id+"F0.imprint","IMPRINT",FACE,{"disambiguationData":[TD([[makeQuery(id+"F0.imprint","IMPRINT",EDGE,{"derivedFrom":sQuery(id+"F0.wireOp",EDGE,"E18.3.0")}),1.0]])]});
            var Q33;
            Q33=makeQuery(id+"F0.imprint","IMPRINT",FACE,{"disambiguationData":[TD([[makeQuery(id+"F0.imprint","IMPRINT",EDGE,{"derivedFrom":sQuery(id+"F0.wireOp",EDGE,"E18.4.0")}),1.0]])]});
            var Q34;
            {var subQ0=sQuery(id+"F0.wireOp",EDGE,"E18.5.0");var subQ1=sQuery(id+"F0.wireOp",EDGE,"E7");var subQ2=makeQuery(id+"F0.imprint","INTERSECT",VERTEX,{"disambiguationData":[OD(0.0)],"derivedFrom":[subQ1,subQ0]});Q34=makeQuery(id+"F0.imprint","IMPRINT",FACE,{"disambiguationData":[TD([[makeQuery(id+"F0.imprint","IMPRINT",EDGE,{"disambiguationData":[TD([[subQ2,-1.0]])],"derivedFrom":subQ1}),1.0]])]});}
            var Q35;
            Q35=makeQuery(id+"F0.imprint","IMPRINT",FACE,{"disambiguationData":[TD([[makeQuery(id+"F0.imprint","IMPRINT",EDGE,{"derivedFrom":sQuery(id+"F0.wireOp",EDGE,"E18.6.0")}),1.0]])]});
            var Q36;
            Q36=makeQuery(id+"F0.imprint","IMPRINT",FACE,{"disambiguationData":[TD([[makeQuery(id+"F0.imprint","IMPRINT",EDGE,{"derivedFrom":sQuery(id+"F0.wireOp",EDGE,"E18.7.0")}),1.0]])]});
            var Q37;
            Q37=makeQuery(id+"F0.imprint","IMPRINT",FACE,{"disambiguationData":[TD([[makeQuery(id+"F0.imprint","IMPRINT",EDGE,{"derivedFrom":sQuery(id+"F0.wireOp",EDGE,"E18.9.0")}),1.0]])]});
            var Q38;
            Q38=makeQuery(id+"F0.imprint","IMPRINT",FACE,{"disambiguationData":[TD([[makeQuery(id+"F0.imprint","IMPRINT",EDGE,{"derivedFrom":sQuery(id+"F0.wireOp",EDGE,"E18.10.0")}),1.0]])]});
            var Q39;
            Q39=makeQuery(id+"F0.imprint","IMPRINT",FACE,{"disambiguationData":[TD([[makeQuery(id+"F0.imprint","IMPRINT",EDGE,{"derivedFrom":sQuery(id+"F0.wireOp",EDGE,"E18.8.0")}),1.0]])]});
            var Q40;
            Q40=makeQuery(id+"F0.imprint","IMPRINT",FACE,{"disambiguationData":[TD([[makeQuery(id+"F0.imprint","IMPRINT",EDGE,{"derivedFrom":sQuery(id+"F0.wireOp",EDGE,"E18.11.0")}),1.0]])]});
            var Q41;
            Q41=makeQuery(id+"F0.imprint","IMPRINT",FACE,{"disambiguationData":[TD([[makeQuery(id+"F0.imprint","IMPRINT",EDGE,{"derivedFrom":sQuery(id+"F0.wireOp",EDGE,"E18.12.0")}),1.0]])]});
            var Q42;
            Q42=makeQuery(id+"F0.imprint","IMPRINT",FACE,{"disambiguationData":[TD([[makeQuery(id+"F0.imprint","IMPRINT",EDGE,{"derivedFrom":sQuery(id+"F0.wireOp",EDGE,"E18.13.0")}),1.0]])]});
            var Q43;
            Q43=makeQuery(id+"F0.imprint","IMPRINT",FACE,{"disambiguationData":[TD([[makeQuery(id+"F0.imprint","IMPRINT",EDGE,{"derivedFrom":sQuery(id+"F0.wireOp",EDGE,"E18.14.0")}),1.0]])]});
            var Q44;
            {var subQ0=sQuery(id+"F0.wireOp",EDGE,"E18.15.0");var subQ1=sQuery(id+"F0.wireOp",EDGE,"E8");var subQ2=makeQuery(id+"F0.imprint","INTERSECT",VERTEX,{"disambiguationData":[OD(0.0)],"derivedFrom":[subQ1,subQ0]});Q44=makeQuery(id+"F0.imprint","IMPRINT",FACE,{"disambiguationData":[TD([[makeQuery(id+"F0.imprint","IMPRINT",EDGE,{"disambiguationData":[TD([[subQ2,-1.0]])],"derivedFrom":subQ1}),-1.0]])]});}
            var Q45;
            {var subQ0=sQuery(id+"F0.wireOp",EDGE,"E18.15.0");var subQ1=sQuery(id+"F0.wireOp",EDGE,"E8");var subQ2=makeQuery(id+"F0.imprint","INTERSECT",VERTEX,{"disambiguationData":[OD(0.0)],"derivedFrom":[subQ1,subQ0]});Q45=makeQuery(id+"F0.imprint","IMPRINT",FACE,{"disambiguationData":[TD([[makeQuery(id+"F0.imprint","IMPRINT",EDGE,{"disambiguationData":[TD([[subQ2,-1.0]])],"derivedFrom":subQ1}),1.0]])]});}
            var Q46;
            Q46=makeQuery(id+"F0.imprint","IMPRINT",FACE,{"disambiguationData":[TD([[makeQuery(id+"F0.imprint","IMPRINT",EDGE,{"derivedFrom":sQuery(id+"F0.wireOp",EDGE,"E18.16.0")}),1.0]])]});
            var Q47;
            Q47=makeQuery(id+"F0.imprint","IMPRINT",FACE,{"disambiguationData":[TD([[makeQuery(id+"F0.imprint","IMPRINT",EDGE,{"derivedFrom":sQuery(id+"F0.wireOp",EDGE,"E18.17.0")}),1.0]])]});
            var Q48;
            Q48=makeQuery(id+"F0.imprint","IMPRINT",FACE,{"disambiguationData":[TD([[makeQuery(id+"F0.imprint","IMPRINT",EDGE,{"derivedFrom":sQuery(id+"F0.wireOp",EDGE,"E18.18.0")}),1.0]])]});
            var Q49;
            Q49=makeQuery(id+"F0.imprint","IMPRINT",FACE,{"disambiguationData":[TD([[makeQuery(id+"F0.imprint","IMPRINT",EDGE,{"derivedFrom":sQuery(id+"F0.wireOp",EDGE,"E18.19.0")}),1.0]])]});
            var Q50;
            Q50=makeQuery(id+"F0.imprint","IMPRINT",FACE,{"disambiguationData":[TD([[makeQuery(id+"F0.imprint","IMPRINT",EDGE,{"derivedFrom":sQuery(id+"F0.wireOp",EDGE,"E18.20.0")}),1.0]])]});
            var Q51;
            Q51=makeQuery(id+"F0.imprint","IMPRINT",FACE,{"disambiguationData":[TD([[makeQuery(id+"F0.imprint","IMPRINT",EDGE,{"derivedFrom":sQuery(id+"F0.wireOp",EDGE,"E18.21.0")}),1.0]])]});
            var Q52;
            Q52=makeQuery(id+"F0.imprint","IMPRINT",FACE,{"disambiguationData":[TD([[makeQuery(id+"F0.imprint","IMPRINT",EDGE,{"derivedFrom":sQuery(id+"F0.wireOp",EDGE,"E18.22.0")}),1.0]])]});
            var Q53;
            Q53=makeQuery(id+"F0.imprint","IMPRINT",FACE,{"disambiguationData":[TD([[makeQuery(id+"F0.imprint","IMPRINT",EDGE,{"derivedFrom":sQuery(id+"F0.wireOp",EDGE,"E18.23.0")}),1.0]])]});
            var Q54;
            Q54=makeQuery(id+"F0.imprint","IMPRINT",FACE,{"disambiguationData":[TD([[makeQuery(id+"F0.imprint","IMPRINT",EDGE,{"derivedFrom":sQuery(id+"F0.wireOp",EDGE,"E18.24.0")}),1.0]])]});
            var Q55;
            {var subQ0=sQuery(id+"F0.wireOp",EDGE,"E18.25.0");var subQ1=sQuery(id+"F0.wireOp",EDGE,"E7");var subQ2=makeQuery(id+"F0.imprint","INTERSECT",VERTEX,{"disambiguationData":[OD(0.0)],"derivedFrom":[subQ1,subQ0]});Q55=makeQuery(id+"F0.imprint","IMPRINT",FACE,{"disambiguationData":[TD([[makeQuery(id+"F0.imprint","IMPRINT",EDGE,{"disambiguationData":[TD([[subQ2,-1.0]])],"derivedFrom":subQ1}),-1.0]])]});}
            var Q56;
            {var subQ0=sQuery(id+"F0.wireOp",EDGE,"E18.25.0");var subQ1=sQuery(id+"F0.wireOp",EDGE,"E7");var subQ2=makeQuery(id+"F0.imprint","INTERSECT",VERTEX,{"disambiguationData":[OD(0.0)],"derivedFrom":[subQ1,subQ0]});Q56=makeQuery(id+"F0.imprint","IMPRINT",FACE,{"disambiguationData":[TD([[makeQuery(id+"F0.imprint","IMPRINT",EDGE,{"disambiguationData":[TD([[subQ2,-1.0]])],"derivedFrom":subQ1}),1.0]])]});}
            var Q57;
            Q57=makeQuery(id+"F0.imprint","IMPRINT",FACE,{"disambiguationData":[TD([[makeQuery(id+"F0.imprint","IMPRINT",EDGE,{"derivedFrom":sQuery(id+"F0.wireOp",EDGE,"E18.26.0")}),1.0]])]});
            var Q58;
            Q58=makeQuery(id+"F0.imprint","IMPRINT",FACE,{"disambiguationData":[TD([[makeQuery(id+"F0.imprint","IMPRINT",EDGE,{"derivedFrom":sQuery(id+"F0.wireOp",EDGE,"E18.27.0")}),1.0]])]});
            var Q59;
            Q59=makeQuery(id+"F0.imprint","IMPRINT",FACE,{"disambiguationData":[TD([[makeQuery(id+"F0.imprint","IMPRINT",EDGE,{"derivedFrom":sQuery(id+"F0.wireOp",EDGE,"E18.28.0")}),1.0]])]});
            var Q60;
            Q60=makeQuery(id+"F0.imprint","IMPRINT",FACE,{"disambiguationData":[TD([[makeQuery(id+"F0.imprint","IMPRINT",EDGE,{"derivedFrom":sQuery(id+"F0.wireOp",EDGE,"E18.29.0")}),1.0]])]});
            var Q61;
            Q61=makeQuery(id+"F0.imprint","IMPRINT",FACE,{"disambiguationData":[TD([[makeQuery(id+"F0.imprint","IMPRINT",EDGE,{"derivedFrom":sQuery(id+"F0.wireOp",EDGE,"E18.30.0")}),1.0]])]});
            var Q62;
            Q62=makeQuery(id+"F0.imprint","IMPRINT",FACE,{"disambiguationData":[TD([[makeQuery(id+"F0.imprint","IMPRINT",EDGE,{"derivedFrom":sQuery(id+"F0.wireOp",EDGE,"E18.31.0")}),1.0]])]});
            var Q63;
            Q63=makeQuery(id+"F0.imprint","IMPRINT",FACE,{"disambiguationData":[TD([[makeQuery(id+"F0.imprint","IMPRINT",EDGE,{"derivedFrom":sQuery(id+"F0.wireOp",EDGE,"E18.32.0")}),1.0]])]});
            var Q64;
            Q64=makeQuery(id+"F0.imprint","IMPRINT",FACE,{"disambiguationData":[TD([[makeQuery(id+"F0.imprint","IMPRINT",EDGE,{"derivedFrom":sQuery(id+"F0.wireOp",EDGE,"E18.34.0")}),1.0]])]});
            var Q65;
            Q65=makeQuery(id+"F0.imprint","IMPRINT",FACE,{"disambiguationData":[TD([[makeQuery(id+"F0.imprint","IMPRINT",EDGE,{"derivedFrom":sQuery(id+"F0.wireOp",EDGE,"E18.33.0")}),1.0]])]});
            var Q66;
            {var subQ0=sQuery(id+"F0.wireOp",EDGE,"E18.35.0");var subQ1=sQuery(id+"F0.wireOp",EDGE,"E8");var subQ2=makeQuery(id+"F0.imprint","INTERSECT",VERTEX,{"disambiguationData":[OD(0.0)],"derivedFrom":[subQ1,subQ0]});Q66=makeQuery(id+"F0.imprint","IMPRINT",FACE,{"disambiguationData":[TD([[makeQuery(id+"F0.imprint","IMPRINT",EDGE,{"disambiguationData":[TD([[subQ2,-1.0]])],"derivedFrom":subQ1}),-1.0]])]});}
            var Q67;
            {var subQ0=sQuery(id+"F0.wireOp",EDGE,"E18.35.0");var subQ1=sQuery(id+"F0.wireOp",EDGE,"E8");var subQ2=makeQuery(id+"F0.imprint","INTERSECT",VERTEX,{"disambiguationData":[OD(0.0)],"derivedFrom":[subQ1,subQ0]});Q67=makeQuery(id+"F0.imprint","IMPRINT",FACE,{"disambiguationData":[TD([[makeQuery(id+"F0.imprint","IMPRINT",EDGE,{"disambiguationData":[TD([[subQ2,-1.0]])],"derivedFrom":subQ1}),1.0]])]});}
            var Q68;
            Q68=makeQuery(id+"F0.imprint","IMPRINT",FACE,{"disambiguationData":[TD([[makeQuery(id+"F0.imprint","IMPRINT",EDGE,{"derivedFrom":sQuery(id+"F0.wireOp",EDGE,"E18.36.0")}),1.0]])]});
            var Q69;
            Q69=makeQuery(id+"F0.imprint","IMPRINT",FACE,{"disambiguationData":[TD([[makeQuery(id+"F0.imprint","IMPRINT",EDGE,{"derivedFrom":sQuery(id+"F0.wireOp",EDGE,"E18.37.0")}),1.0]])]});
            var Q70;
            Q70=makeQuery(id+"F0.imprint","IMPRINT",FACE,{"disambiguationData":[TD([[makeQuery(id+"F0.imprint","IMPRINT",EDGE,{"derivedFrom":sQuery(id+"F0.wireOp",EDGE,"E18.38.0")}),1.0]])]});
            var Q71;
            Q71=makeQuery(id+"F0.imprint","IMPRINT",FACE,{"disambiguationData":[TD([[makeQuery(id+"F0.imprint","IMPRINT",EDGE,{"derivedFrom":sQuery(id+"F0.wireOp",EDGE,"E18.39.0")}),1.0]])]});
            var Q72;
            {var subQ0=sQuery(id+"F0.wireOp",EDGE,"E8");var subQ1=sQuery(id+"F0.wireOp",EDGE,"E0");var subQ2=makeQuery(id+"F0.imprint","INTERSECT",VERTEX,{"disambiguationData":[OD(0.0)],"derivedFrom":[subQ1,subQ0]});Q72=makeQuery(id+"F0.imprint","IMPRINT",FACE,{"disambiguationData":[TD([[makeQuery(id+"F0.imprint","IMPRINT",EDGE,{"disambiguationData":[TD([[subQ2,1.0]])],"derivedFrom":subQ1}),-1.0]])]});}
            var Q73;
            {var subQ0=sQuery(id+"F0.wireOp",EDGE,"E7");var subQ1=sQuery(id+"F0.wireOp",EDGE,"E0");var subQ2=makeQuery(id+"F0.imprint","INTERSECT",VERTEX,{"disambiguationData":[OD(0.0)],"derivedFrom":[subQ1,subQ0]});Q73=makeQuery(id+"F0.imprint","IMPRINT",FACE,{"disambiguationData":[TD([[makeQuery(id+"F0.imprint","IMPRINT",EDGE,{"disambiguationData":[TD([[subQ2,1.0]])],"derivedFrom":subQ1}),-1.0]])]});}
            var Q74;
            {var subQ0=sQuery(id+"F0.wireOp",EDGE,"E7");var subQ1=sQuery(id+"F0.wireOp",EDGE,"E0");var subQ2=makeQuery(id+"F0.imprint","INTERSECT",VERTEX,{"disambiguationData":[OD(0.0)],"derivedFrom":[subQ1,subQ0]});Q74=makeQuery(id+"F0.imprint","IMPRINT",FACE,{"disambiguationData":[TD([[makeQuery(id+"F0.imprint","IMPRINT",EDGE,{"disambiguationData":[TD([[subQ2,-1.0]])],"derivedFrom":subQ1}),-1.0]])]});}
            var Q75;
            {var subQ0=sQuery(id+"F0.wireOp",EDGE,"E8");var subQ1=sQuery(id+"F0.wireOp",EDGE,"E0");var subQ2=makeQuery(id+"F0.imprint","INTERSECT",VERTEX,{"disambiguationData":[OD(1.0)],"derivedFrom":[subQ1,subQ0]});Q75=makeQuery(id+"F0.imprint","IMPRINT",FACE,{"disambiguationData":[TD([[makeQuery(id+"F0.imprint","IMPRINT",EDGE,{"disambiguationData":[TD([[subQ2,-1.0]])],"derivedFrom":subQ1}),-1.0]])]});}
            extrude(context, id + "F2", {"entities" : qUnion([Q0, Q1, Q2, Q3, Q4, Q5, Q6, Q7, Q8, Q9, Q10, Q11, Q12, Q13, Q14, Q15, Q16, Q17, Q18, Q19, Q20, Q21, Q22, Q23, Q24, Q25, Q26, Q27, Q28, Q29, Q30, Q31, Q32, Q33, Q34, Q35, Q36, Q37, Q38, Q39, Q40, Q41, Q42, Q43, Q44, Q45, Q46, Q47, Q48, Q49, Q50, Q51, Q52, Q53, Q54, Q55, Q56, Q57, Q58, Q59, Q60, Q61, Q62, Q63, Q64, Q65, Q66, Q67, Q68, Q69, Q70, Q71, Q72, Q73, Q74, Q75]), "depth" : 7 * mm, "offsetDistance" : 25 * mm});
        }
    });
